# Revit family: Gleitplatte 2x Anschluß Zollmaße
name_source: partatom
category: HLS-Bauteile
units: mm (PartAtom-declared; Revit-internal decimal feet)

## family parameters
Arbeitsebenenbasiert = Ja
Beim Laden mit Abzugskörper schneiden = Nein
Bemaßung runder Anschluss = Durchmesser verwenden
Beschriftungsausrichtung beibehalten = Nein
Gemeinsam genutzt = Ja
Immer vertikal = Nein
OmniClass-Nummer = 23.75.00.00
OmniClass-Titel = Climate Control (HVAC)
Raumberechnungspunkt = Nein
Teiletyp = Normal

## types (17) — shared parameters
Anzahl Anschlüsse = 2
Fabrikat = MEFA
Firma = MEFA Befestigungs- und Montagesysteme GmbH
Material = Stahl
Materialname = S235
Mengeneinheit = St
vpe = 1
zero-valued in all types: Vorgabe-Ansicht

## per-type parameters (varying)
| type | Abstand zur Außenkante | Achsmaß | Anschluss | Anschlüsse | Artikelnummer | Breite | EAN | Gewicht | Gewicht pro Bauteil | Höhe Gewindeanschluss HGW | Kurztext1 | Kurztext2 | Länge | Stärke | max. Schiebeweg axial hängend | max. Schiebeweg axial stehend | max. zul. Last |
| Gleitplatte 200x100x 8, 2x 1/2" | 25 mm  [stored 0.082021 ft] | 25 mm | 1'' | Runde Gewindeanschlusse parametrik : Muffe 1´´ (0009881) | 0771811 | 200 mm  [stored 0.656168 ft] | 4250928418364 | 4.95 kg | 4.95 kg | 20 mm  [stored 0.0656168 ft] | Gleitplatte 300 x 200 x 10 | Anschluss 2 x 1'' | 300 mm | 10 mm  [stored 0.0328084 ft] | 160 mm  [stored 0.524934 ft] | 250 mm | 5.60 kN |
| Gleitplatte 200x150x 8, 2x 1/2" | 25 mm  [stored 0.082021 ft] | 25 mm | 1/2'' | Runde Gewindeanschlusse parametrik : Muffe 1/2´´ (0009865) | 0771331 | 150 mm | 4250928418296 | 1.98 kg | 1.98 kg | 15 mm  [stored 0.0492126 ft] | Gleitplatte 200 x 150 x 8 | Anschluss 2 x 1/2'' | 200 mm  [stored 0.656168 ft] | 8 mm  [stored 0.0262467 ft] | 70 mm | 150 mm | 4.40 kN |
| Gleitplatte 250x100x 8, 2x 1/2" | 25 mm  [stored 0.082021 ft] | 25 mm | 1/2'' | Runde Gewindeanschlusse parametrik : Muffe 1/2´´ (0009865) | 0771503 | 100 mm  [stored 0.328084 ft] | 4250928418319 | 1.66 kg | 1.66 kg | 15 mm  [stored 0.0492126 ft] | Gleitplatte 250 x 100 x 8 | Anschluss 2 x 1/2'' | 250 mm | 8 mm  [stored 0.0262467 ft] | 120 mm | 200 mm  [stored 0.656168 ft] | 2.20 kN |
| Gleitplatte 250x200x10, 2x 1/2" | 25 mm  [stored 0.082021 ft] | 25 mm | 1/2'' | Runde Gewindeanschlusse parametrik : Muffe 1/2´´ (0009865) | 0771710 | 200 mm  [stored 0.656168 ft] | 4250928418357 | 4.06 kg | 4.06 kg | 15 mm  [stored 0.0492126 ft] | Gleitplatte 250 x 200 x 10 | Anschluss 2 x 1/2'' | 250 mm | 10 mm  [stored 0.0328084 ft] | 120 mm | 200 mm  [stored 0.656168 ft] | 6.40 kN |
| Gleitplatte 150x100x 8, 2x 1/2" | 25 mm  [stored 0.082021 ft] | 25 mm | 1/2'' | Runde Gewindeanschlusse parametrik : Muffe 1/2´´ (0009865) | 0771202 | 100 mm  [stored 0.328084 ft] | 4250928418241 | 1.02 kg | 1.02 kg | 15 mm  [stored 0.0492126 ft] | Gleitplatte 150 x 100 x 8 | Anschluss 2 x 1/2'' | 150 mm | 8 mm  [stored 0.0262467 ft] | 20 mm  [stored 0.0656168 ft] | 100 mm  [stored 0.328084 ft] | 4.80 kN |
| Gleitplatte 150x100x 8, 2x 3/4" | 25 mm  [stored 0.082021 ft] | 25 mm | 3/4'' | Runde Gewindeanschlusse parametrik : Schweißmuffe 3/4´´ (0009873) | 0771229 | 100 mm  [stored 0.328084 ft] | 4250928418272 | 1.05 kg | 1.05 kg | 15 mm  [stored 0.0492126 ft] | Gleitplatte 150 x 100 x 8 | Anschluss 2 x 3/4'' | 150 mm | 8 mm  [stored 0.0262467 ft] | 20 mm  [stored 0.0656168 ft] | 100 mm  [stored 0.328084 ft] | 4.80 kN |
| Gleitplatte 200x100x 8, 2x 3/4" | 25 mm  [stored 0.082021 ft] | 25 mm | 3/4'' | Runde Gewindeanschlusse parametrik : Schweißmuffe 3/4´´ (0009873) | 0771228 | 100 mm  [stored 0.328084 ft] | 4250928418265 | 1.37 kg | 1.37 kg | 15 mm  [stored 0.0492126 ft] | Gleitplatte 200 x 100 x 8 | Anschluss 2 x 3/4'' | 200 mm  [stored 0.656168 ft] | 8 mm  [stored 0.0262467 ft] | 70 mm | 150 mm | 3.00 kN |
| Gleitplatte 200x100x 8, 2x 1" | 25 mm  [stored 0.082021 ft] | 25 mm | 1'' | Runde Gewindeanschlusse parametrik : Muffe 1´´ (0009881) | 0771236 | 100 mm  [stored 0.328084 ft] | 4250928418289 | 1.44 kg | 1.44 kg | 15 mm  [stored 0.0492126 ft] | Gleitplatte 200 x 100 x 8 | Anschluss 2 x 1'' | 200 mm  [stored 0.656168 ft] | 8 mm  [stored 0.0262467 ft] | 70 mm | 150 mm | 3.00 kN |
| Gleitplatte 250x100x 8, 2x 3/4" | 25 mm  [stored 0.082021 ft] | 25 mm | 3/4'' | Runde Gewindeanschlusse parametrik : Schweißmuffe 3/4´´ (0009873) | 0771511 | 100 mm  [stored 0.328084 ft] | 4250928418326 | 1.68 kg | 1.68 kg | 15 mm  [stored 0.0492126 ft] | Gleitplatte 250 x 100 x 8 | Anschluss 2 x 3/4'' | 250 mm | 8 mm  [stored 0.0262467 ft] | 120 mm | 200 mm  [stored 0.656168 ft] | 2.20 kN |
| Gleitplatte 250x100x 8, 2x 1" | 25 mm  [stored 0.082021 ft] | 25 mm | 1'' | Runde Gewindeanschlusse parametrik : Muffe 1´´ (0009881) | 0771538 | 100 mm  [stored 0.328084 ft] | 4250928418333 | 1.75 kg | 1.75 kg | 15 mm  [stored 0.0492126 ft] | Gleitplatte 250 x 100 x 8 | Anschluss 2 x 1'' | 250 mm | 8 mm  [stored 0.0262467 ft] | 120 mm | 200 mm  [stored 0.656168 ft] | 2.20 kN |
| Gleitplatte 250x200x 8, 2x 1/2" | 25 mm  [stored 0.082021 ft] | 25 mm | 1/2'' | Runde Gewindeanschlusse parametrik : Muffe 1/2´´ (0009865) | 0771707 | 200 mm  [stored 0.656168 ft] | 4250928418340 | 3.26 kg | 3.26 kg | 15 mm  [stored 0.0492126 ft] | Gleitplatte 250 x 200 x 8 | Anschluss 2 x 1/2'' | 250 mm | 8 mm  [stored 0.0262467 ft] | 120 mm | 200 mm  [stored 0.656168 ft] | 4.20 kN |
| Gleitplatte 300x200x10, 2x 1" | 25 mm  [stored 0.082021 ft] | 25 mm | 1'' | Runde Gewindeanschlusse parametrik : Muffe 1´´ (0009881) | 0771811 | 200 mm  [stored 0.656168 ft] | 4250928418364 | 4.95 kg | 4.95 kg | 20 mm  [stored 0.0656168 ft] | Gleitplatte 300 x 200 x 10 | Anschluss 2 x 1'' | 300 mm | 10 mm  [stored 0.0328084 ft] | 160 mm  [stored 0.524934 ft] | 250 mm | 5.60 kN |
| Gleitplatte 300x200x12, 2x 1" | 25 mm  [stored 0.082021 ft] | 25 mm | 1'' | Runde Gewindeanschlusse parametrik : Muffe 1´´ (0009881) | 0771814 | 200 mm  [stored 0.656168 ft] | 4250928418371 | 5.91 kg | 5.91 kg | 20 mm  [stored 0.0656168 ft] | Gleitplatte 300 x 200 x 12 | Anschluss 2 x 1'' | 300 mm | 12 mm  [stored 0.0393701 ft] | 160 mm  [stored 0.524934 ft] | 250 mm | 8.10 kN |
| Gleitplatte 300x250x12, 2x 1" | 25 mm  [stored 0.082021 ft] | 25 mm | 1'' | Runde Gewindeanschlusse parametrik : Muffe 1´´ (0009881) | 0771817 | 250 mm | 4250928418388 | 7.35 kg | 7.35 kg | 20 mm  [stored 0.0656168 ft] | Gleitplatte 300 x 250 x 12 | Anschluss 2 x 1'' | 300 mm | 12 mm  [stored 0.0393701 ft] | 160 mm  [stored 0.524934 ft] | 250 mm | 10.20 kN |
| Gleitplatte 350x250x12, 2x 1" | 25 mm  [stored 0.082021 ft] | 25 mm | 1'' | Runde Gewindeanschlusse parametrik : Muffe 1´´ (0009881) | 0771911 | 250 mm | 4250928418401 | 8.55 kg | 8.55 kg | 20 mm  [stored 0.0656168 ft] | Gleitplatte 350 x 250 x 12 | Anschluss 2 x 1'' | 350 mm | 12 mm  [stored 0.0393701 ft] | 200 mm  [stored 0.656168 ft] | 300 mm | 7.40 kN |
| Gleitplatte 350x200x12, 2x 1 1/4" | 35 mm | 35 mm | 1 1/4'' | Runde Gewindeanschlusse parametrik : Muffe 1 1/4´´ (0009898) | 0771902 | 200 mm  [stored 0.656168 ft] | 4250928418395 | 6.93 kg | 6.93 kg | 20 mm  [stored 0.0656168 ft] | Gleitplatte 350 x 200 x 12 | Anschluss 2 x 1 1/4'' | 350 mm | 12 mm  [stored 0.0393701 ft] | 200 mm  [stored 0.656168 ft] | 300 mm | 6.00 kN |
| Gleitplatte 400x250x12, 2x 1 1/4" | 35 mm | 35 mm | 1 1/4'' | Runde Gewindeanschlusse parametrik : Muffe 1 1/4´´ (0009898) | 0771973 | 250 mm | 4250928418418 | 9.81 kg | 9.81 kg | 20 mm  [stored 0.0656168 ft] | Gleitplatte 350 x 250 x 12 | Anschluss 2 x 1 1/4'' | 400 mm  [stored 1.31234 ft] | 12 mm  [stored 0.0393701 ft] | 250 mm | 350 mm | 5.40 kN |

note: [stored X ft] marks values corroborated as IEEE doubles in the binary element streams (Revit-internal decimal feet)

## geometry (parser evidence)
native form markers: Sweep x3
no freeform markers — native parametric forms only
